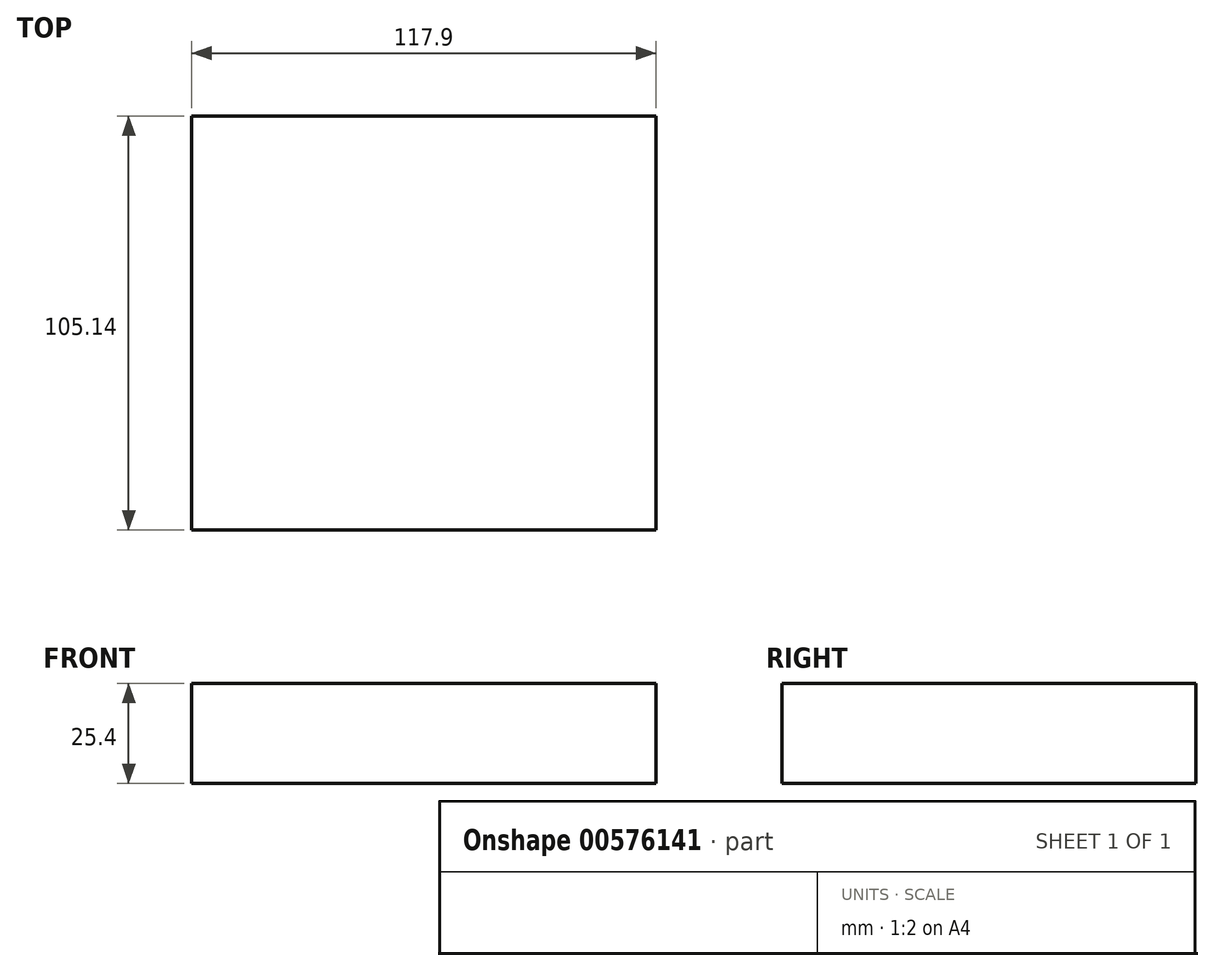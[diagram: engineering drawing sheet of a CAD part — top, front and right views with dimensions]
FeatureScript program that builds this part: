
annotation { "Feature Type Name" : "Feature", "Feature Type Description" : "" }
export const myFeature = defineFeature(function(context is Context, id is Id, definition is map)
    precondition{}
    {
        {
            var Q0;
            Q0=qCreatedBy(makeId("Top.planeOp"),FACE);
            var sketch = newSketch(context, id + "F0", { "sketchPlane" : qUnion([Q0])});
            skLineSegment(sketch, "E0.bottom", {"start": v(-56.05, 55.86) * mm, "end": v(61.85, 55.86) * mm});
            skLineSegment(sketch, "E0.top", {"start": v(-56.05, -49.28) * mm, "end": v(61.85, -49.28) * mm});
            skLineSegment(sketch, "E0.left", {"start": v(-56.05, 55.86) * mm, "end": v(-56.05, -49.28) * mm});
            skLineSegment(sketch, "E0.right", {"start": v(61.85, 55.86) * mm, "end": v(61.85, -49.28) * mm});
            skSolve(sketch);
        }
        {
            var Q0;
            Q0=makeQuery(id+"F0.imprint","IMPRINT",FACE,{"disambiguationData":[TD([[makeQuery(id+"F0.imprint","IMPRINT",EDGE,{"derivedFrom":sQuery(id+"F0.wireOp",EDGE,"E0.bottom")}),-1.0]])]});
            extrude(context, id + "F1", {"entities" : qUnion([Q0]), "endBound" : BoundingType.SYMMETRIC, "depth" : 25.4 * mm, "offsetDistance" : 25.4 * mm});
        }
    });
